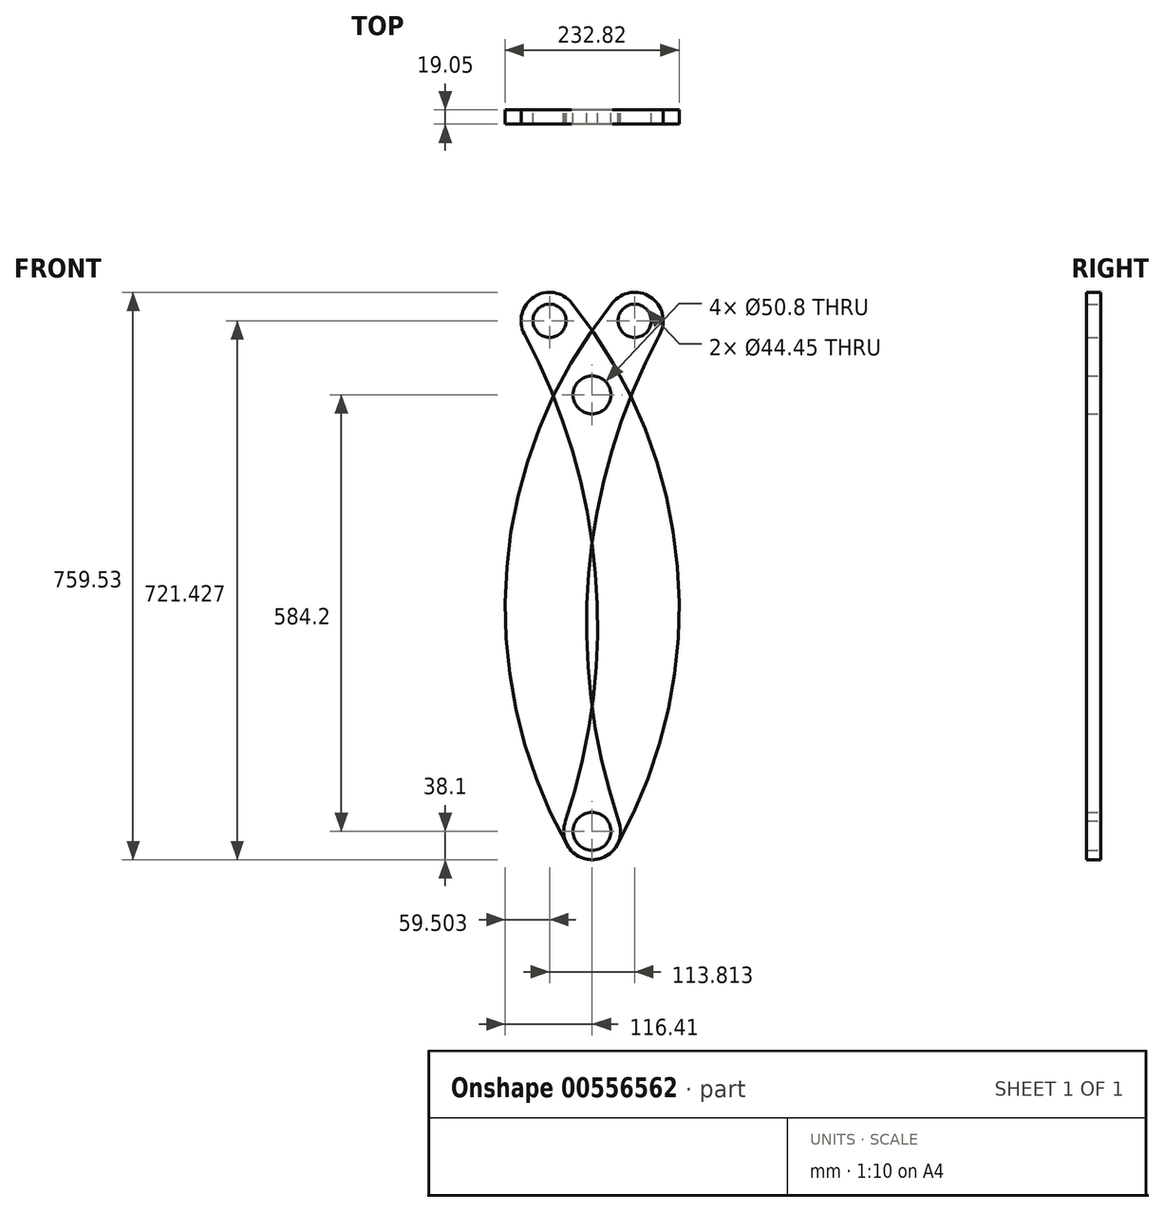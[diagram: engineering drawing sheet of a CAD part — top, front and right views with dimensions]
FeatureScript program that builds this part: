
annotation { "Feature Type Name" : "Feature", "Feature Type Description" : "" }
export const myFeature = defineFeature(function(context is Context, id is Id, definition is map)
    precondition{}
    {
        {
            var Q0;
            Q0=qCreatedBy(makeId("Front.planeOp"),FACE);
            var sketch = newSketch(context, id + "F0", { "sketchPlane" : qUnion([Q0])});
            skCircle(sketch, "E0", {"center": v(0, -584.2) * mm, "radius": 25.4 * mm});
            skCircle(sketch, "E1", {"center": v(0, 0) * mm, "radius": 25.4 * mm});
            skArc(sketch, "E2", {"start": v(-33.23, -602.84) * mm, "mid": v(16.32, -618.63) * mm, "end": v(35.47, -570.3) * mm});
            skArc(sketch, "E3", {"start": v(35.47, -13.9) * mm, "mid": v(16.32, 34.43) * mm, "end": v(-33.23, 18.64) * mm, "construction": true});
            skArc(sketch, "E4", {"start": v(-33.23, 18.64) * mm, "mid": v(-114.45, -292.1) * mm, "end": v(-33.23, -602.84) * mm, "construction": true});
            skArc(sketch, "E5", {"start": v(35.47, -13.9) * mm, "mid": v(-17.13, -292.1) * mm, "end": v(35.47, -570.3) * mm, "construction": true});
            skCircle(sketch, "E6", {"center": v(520.55, -292.1) * mm, "radius": 635 * mm, "construction": true});
            skCircle(sketch, "E7", {"center": v(744.87, -292.1) * mm, "radius": 762 * mm, "construction": true});
            skArc(sketch, "E8", {"start": v(80.53, 81.11) * mm, "mid": v(56.9, 99.13) * mm, "end": v(29.44, 110.44) * mm, "construction": true});
            skCircle(sketch, "E9", {"center": v(56.9, 99.13) * mm, "radius": 22.23 * mm});
            skArc(sketch, "E10", {"start": v(90.48, 81.11) * mm, "mid": v(77.94, 130.9) * mm, "end": v(27.22, 123.01) * mm});
            skArc(sketch, "E11", {"start": v(90.48, 81.11) * mm, "mid": v(-4.43, -238.9) * mm, "end": v(35.47, -570.3) * mm});
            skArc(sketch, "E12", {"start": v(27.22, 123.01) * mm, "mid": v(-114.17, -230.66) * mm, "end": v(-33.23, -602.84) * mm});
            skSolve(sketch);
        }
        {
            var Q0;
            Q0=makeQuery(id+"F0.imprint","IMPRINT",FACE,{"disambiguationData":[TD([[makeQuery(id+"F0.imprint","IMPRINT",EDGE,{"derivedFrom":sQuery(id+"F0.wireOp",EDGE,"E1")}),-1.0]])]});
            extrude(context, id + "F1", {"entities" : qUnion([Q0]), "depth" : 19.05 * mm, "offsetDistance" : 25.4 * mm});
        }
        {
            var Q0;
            Q0=makeQuery(id+"F1.opExtrude","SWEPT_BODY",BODY,{"disambiguationData":[OSD([sQuery(id+"F0.wireOp",EDGE,"E1"),sQuery(id+"F0.wireOp",EDGE,"E2"),sQuery(id+"F0.wireOp",EDGE,"E0"),sQuery(id+"F0.wireOp",EDGE,"E9"),sQuery(id+"F0.wireOp",EDGE,"E10"),sQuery(id+"F0.wireOp",EDGE,"E11"),sQuery(id+"F0.wireOp",EDGE,"E12")])]});
            var Q1;
            Q1=qCreatedBy(makeId("Right.planeOp"),FACE);
            mirror(context, id + "F2", {"entities" : qUnion([Q0]), "mirrorPlane" : qUnion([Q1])});
        }
    });
